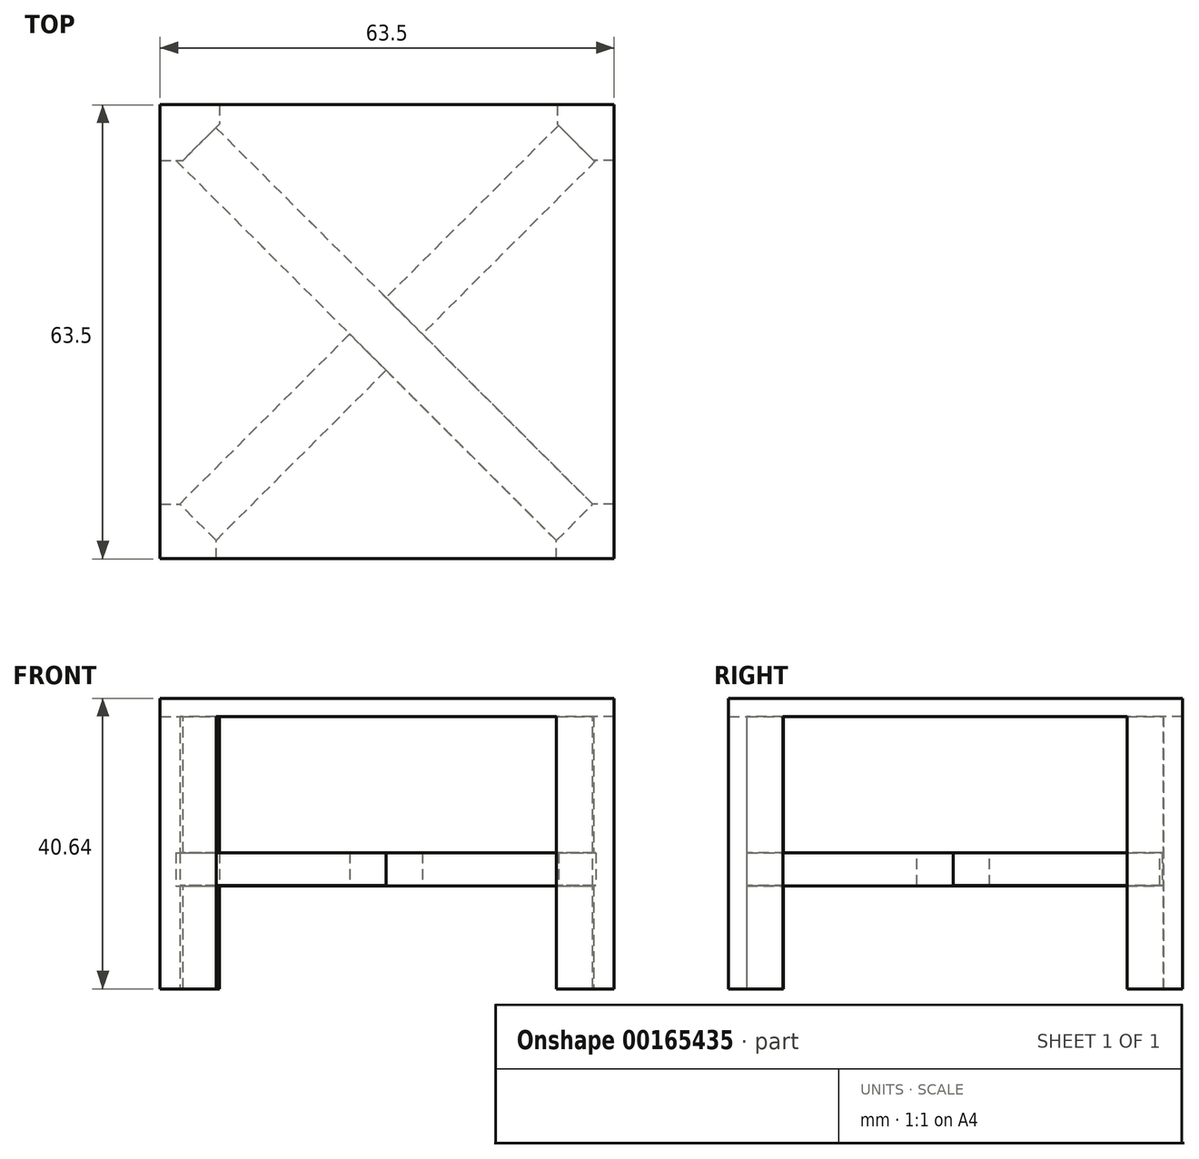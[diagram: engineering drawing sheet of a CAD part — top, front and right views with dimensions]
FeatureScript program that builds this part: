
annotation { "Feature Type Name" : "Feature", "Feature Type Description" : "" }
export const myFeature = defineFeature(function(context is Context, id is Id, definition is map)
    precondition{}
    {
        {
            var Q0;
            Q0=qCreatedBy(makeId("Top.planeOp"),FACE);
            var sketch = newSketch(context, id + "F0", { "sketchPlane" : qUnion([Q0])});
            skLineSegment(sketch, "E0.bottom", {"start": v(-28.63, 27.36) * mm, "end": v(34.87, 27.36) * mm});
            skLineSegment(sketch, "E0.top", {"start": v(-28.63, -36.14) * mm, "end": v(34.87, -36.14) * mm});
            skLineSegment(sketch, "E0.left", {"start": v(-28.63, 27.36) * mm, "end": v(-28.63, -36.14) * mm});
            skLineSegment(sketch, "E0.right", {"start": v(34.87, 27.36) * mm, "end": v(34.87, -36.14) * mm});
            skSolve(sketch);
        }
        {
            var Q0;
            Q0=makeQuery(id+"F0.imprint","IMPRINT",FACE,{"disambiguationData":[TD([[makeQuery(id+"F0.imprint","IMPRINT",EDGE,{"derivedFrom":sQuery(id+"F0.wireOp",EDGE,"E0.bottom")}),-1.0]])]});
            extrude(context, id + "F1", {"entities" : qUnion([Q0]), "depth" : 2.54 * mm});
        }
        {
            var Q0;
            Q0=makeQuery(id+"F1.opExtrude","CAP_FACE",FACE,{"disambiguationData":[OSD([sQuery(id+"F0.wireOp",EDGE,"E0.bottom"),sQuery(id+"F0.wireOp",EDGE,"E0.top"),sQuery(id+"F0.wireOp",EDGE,"E0.left"),sQuery(id+"F0.wireOp",EDGE,"E0.right")])],"isStart":true});
            var sketch = newSketch(context, id + "F2", { "sketchPlane" : qUnion([Q0])});
            skLineSegment(sketch, "E1.bottom", {"start": v(-28.63, 36.14) * mm, "end": v(-20.8, 36.14) * mm});
            skLineSegment(sketch, "E1.top", {"start": v(-28.63, 28.48) * mm, "end": v(-20.8, 28.48) * mm});
            skLineSegment(sketch, "E1.left", {"start": v(-28.63, 36.14) * mm, "end": v(-28.63, 28.48) * mm});
            skLineSegment(sketch, "E1.right", {"start": v(-20.8, 36.14) * mm, "end": v(-20.8, 28.48) * mm});
            skSolve(sketch);
        }
        {
            var Q0;
            Q0 = qSketchRegion(id + "F2", true);
            extrude(context, id + "F3", {"entities" : qUnion([Q0]), "operationType" : NewBodyOperationType.ADD, "depth" : 38.1 * mm});
        }
        {
            var Q0;
            Q0=makeQuery(id+"F1.opExtrude","CAP_FACE",FACE,{"disambiguationData":[OSD([sQuery(id+"F0.wireOp",EDGE,"E0.bottom"),sQuery(id+"F0.wireOp",EDGE,"E0.top"),sQuery(id+"F0.wireOp",EDGE,"E0.left"),sQuery(id+"F0.wireOp",EDGE,"E0.right")])],"isStart":true});
            var sketch = newSketch(context, id + "F4", { "sketchPlane" : qUnion([Q0])});
            skLineSegment(sketch, "E2.bottom", {"start": v(-28.63, -27.36) * mm, "end": v(-20.34, -27.36) * mm});
            skLineSegment(sketch, "E2.top", {"start": v(-28.63, -19.58) * mm, "end": v(-20.34, -19.58) * mm});
            skLineSegment(sketch, "E2.left", {"start": v(-28.63, -27.36) * mm, "end": v(-28.63, -19.58) * mm});
            skLineSegment(sketch, "E2.right", {"start": v(-20.34, -27.36) * mm, "end": v(-20.34, -19.58) * mm});
            skSolve(sketch);
        }
        {
            var Q0;
            Q0=makeQuery(id+"F4.imprint","IMPRINT",FACE,{"disambiguationData":[TD([[makeQuery(id+"F4.imprint","IMPRINT",EDGE,{"derivedFrom":sQuery(id+"F4.wireOp",EDGE,"E2.bottom")}),1.0]])]});
            extrude(context, id + "F5", {"entities" : qUnion([Q0]), "operationType" : NewBodyOperationType.ADD, "depth" : 38.1 * mm});
        }
        {
            var Q0;
            Q0=makeQuery(id+"F1.opExtrude","CAP_FACE",FACE,{"disambiguationData":[OSD([sQuery(id+"F0.wireOp",EDGE,"E0.bottom"),sQuery(id+"F0.wireOp",EDGE,"E0.top"),sQuery(id+"F0.wireOp",EDGE,"E0.left"),sQuery(id+"F0.wireOp",EDGE,"E0.right")])],"isStart":true});
            var sketch = newSketch(context, id + "F6", { "sketchPlane" : qUnion([Q0])});
            skLineSegment(sketch, "E3.bottom", {"start": v(34.87, -27.36) * mm, "end": v(26.91, -27.36) * mm});
            skLineSegment(sketch, "E3.top", {"start": v(34.87, -19.57) * mm, "end": v(26.91, -19.57) * mm});
            skLineSegment(sketch, "E3.left", {"start": v(34.87, -27.36) * mm, "end": v(34.87, -19.57) * mm});
            skLineSegment(sketch, "E3.right", {"start": v(26.91, -27.36) * mm, "end": v(26.91, -19.57) * mm});
            skSolve(sketch);
        }
        {
            var Q0;
            Q0=makeQuery(id+"F6.imprint","IMPRINT",FACE,{"disambiguationData":[TD([[makeQuery(id+"F6.imprint","IMPRINT",EDGE,{"derivedFrom":sQuery(id+"F6.wireOp",EDGE,"E3.bottom")}),1.0]])]});
            extrude(context, id + "F7", {"entities" : qUnion([Q0]), "operationType" : NewBodyOperationType.ADD, "depth" : 38.1 * mm});
        }
        {
            var Q0;
            Q0=makeQuery(id+"F1.opExtrude","CAP_FACE",FACE,{"disambiguationData":[OSD([sQuery(id+"F0.wireOp",EDGE,"E0.bottom"),sQuery(id+"F0.wireOp",EDGE,"E0.top"),sQuery(id+"F0.wireOp",EDGE,"E0.left"),sQuery(id+"F0.wireOp",EDGE,"E0.right")])],"isStart":true});
            var sketch = newSketch(context, id + "F8", { "sketchPlane" : qUnion([Q0])});
            skLineSegment(sketch, "E4.bottom", {"start": v(34.87, 36.14) * mm, "end": v(26.78, 36.14) * mm});
            skLineSegment(sketch, "E4.top", {"start": v(34.87, 28.51) * mm, "end": v(26.78, 28.51) * mm});
            skLineSegment(sketch, "E4.left", {"start": v(34.87, 36.14) * mm, "end": v(34.87, 28.51) * mm});
            skLineSegment(sketch, "E4.right", {"start": v(26.78, 36.14) * mm, "end": v(26.78, 28.51) * mm});
            skSolve(sketch);
        }
        {
            var Q0;
            Q0=makeQuery(id+"F8.imprint","IMPRINT",FACE,{"disambiguationData":[TD([[makeQuery(id+"F8.imprint","IMPRINT",EDGE,{"derivedFrom":sQuery(id+"F8.wireOp",EDGE,"E4.bottom")}),-1.0]])]});
            extrude(context, id + "F9", {"entities" : qUnion([Q0]), "operationType" : NewBodyOperationType.ADD, "depth" : 38.1 * mm});
        }
        {
            var Q0;
            Q0=makeQuery(id+"F3.opExtrude","SWEPT_EDGE",EDGE,{"disambiguationData":[OSD([sQuery(id+"F2.wireOp",EDGE,"E1.top"),sQuery(id+"F2.wireOp",EDGE,"E1.right")])]});
            chamfer(context, id + "F10", {"entities" : qUnion([Q0]), "width" : 5.08 * mm, "tangentPropagation" : true});
        }
        {
            var Q0;
            Q0=makeQuery(id+"F7.opExtrude","SWEPT_EDGE",EDGE,{"disambiguationData":[OSD([sQuery(id+"F6.wireOp",EDGE,"E3.top"),sQuery(id+"F6.wireOp",EDGE,"E3.right")])]});
            chamfer(context, id + "F11", {"entities" : qUnion([Q0]), "width" : 5.08 * mm, "tangentPropagation" : true});
        }
        {
            var Q0;
            Q0=makeQuery(id+"F5.opExtrude","SWEPT_EDGE",EDGE,{"disambiguationData":[OSD([sQuery(id+"F4.wireOp",EDGE,"E2.top"),sQuery(id+"F4.wireOp",EDGE,"E2.right")])]});
            chamfer(context, id + "F12", {"entities" : qUnion([Q0]), "width" : 5.08 * mm, "tangentPropagation" : true});
        }
        {
            var Q0;
            Q0=makeQuery(id+"F9.opExtrude","SWEPT_EDGE",EDGE,{"disambiguationData":[OSD([sQuery(id+"F8.wireOp",EDGE,"E4.top"),sQuery(id+"F8.wireOp",EDGE,"E4.right")])]});
            chamfer(context, id + "F13", {"entities" : qUnion([Q0]), "width" : 5.08 * mm, "tangentPropagation" : true});
        }
        {
            var Q0;
            Q0=makeQuery(id+"F13.opChamfer","BLEND_FACE",FACE,{"disambiguationData":[OSD([sQuery(id+"F8.wireOp",EDGE,"E4.top"),sQuery(id+"F8.wireOp",EDGE,"E4.right")])]});
            var sketch = newSketch(context, id + "F14", { "sketchPlane" : qUnion([Q0])});
            skLineSegment(sketch, "E5.bottom", {"start": v(4.81, -19.05) * mm, "end": v(-2.37, -19.05) * mm});
            skLineSegment(sketch, "E5.top", {"start": v(4.81, -23.73) * mm, "end": v(-2.37, -23.73) * mm});
            skLineSegment(sketch, "E5.left", {"start": v(4.81, -19.05) * mm, "end": v(4.81, -23.73) * mm});
            skLineSegment(sketch, "E5.right", {"start": v(-2.37, -19.05) * mm, "end": v(-2.37, -23.73) * mm});
            skSolve(sketch);
        }
        {
            var Q0;
            Q0=makeQuery(id+"F14.imprint","IMPRINT",FACE,{"disambiguationData":[TD([[makeQuery(id+"F14.imprint","IMPRINT",EDGE,{"derivedFrom":sQuery(id+"F14.wireOp",EDGE,"E5.bottom")}),1.0]])]});
            extrude(context, id + "F15", {"entities" : qUnion([Q0]), "operationType" : NewBodyOperationType.ADD, "depth" : 75.95 * mm});
        }
        {
            var Q0;
            Q0=makeQuery(id+"F10.opChamfer","BLEND_FACE",FACE,{"disambiguationData":[OSD([sQuery(id+"F2.wireOp",EDGE,"E1.top"),sQuery(id+"F2.wireOp",EDGE,"E1.right")])]});
            var sketch = newSketch(context, id + "F16", { "sketchPlane" : qUnion([Q0])});
            skLineSegment(sketch, "E6", {"start": v(-9.02, -38.1) * mm, "end": v(-9.02, -23.67) * mm});
            skLineSegment(sketch, "E7", {"start": v(-9.02, -23.67) * mm, "end": v(-1.84, -23.67) * mm});
            skLineSegment(sketch, "E8", {"start": v(-9.02, -23.67) * mm, "end": v(-9.02, -19.05) * mm});
            skLineSegment(sketch, "E9", {"start": v(-9.02, -19.05) * mm, "end": v(-1.84, -19.05) * mm});
            skLineSegment(sketch, "E10", {"start": v(-1.84, -19.05) * mm, "end": v(-1.84, -23.67) * mm});
            skSolve(sketch);
        }
        {
            var Q0;
            Q0=makeQuery(id+"F16.imprint","IMPRINT",FACE,{"disambiguationData":[TD([[makeQuery(id+"F16.imprint","IMPRINT",EDGE,{"derivedFrom":sQuery(id+"F16.wireOp",EDGE,"E7")}),1.0]])]});
            extrude(context, id + "F17", {"entities" : qUnion([Q0]), "operationType" : NewBodyOperationType.ADD, "depth" : 78.23 * mm});
        }
    });
